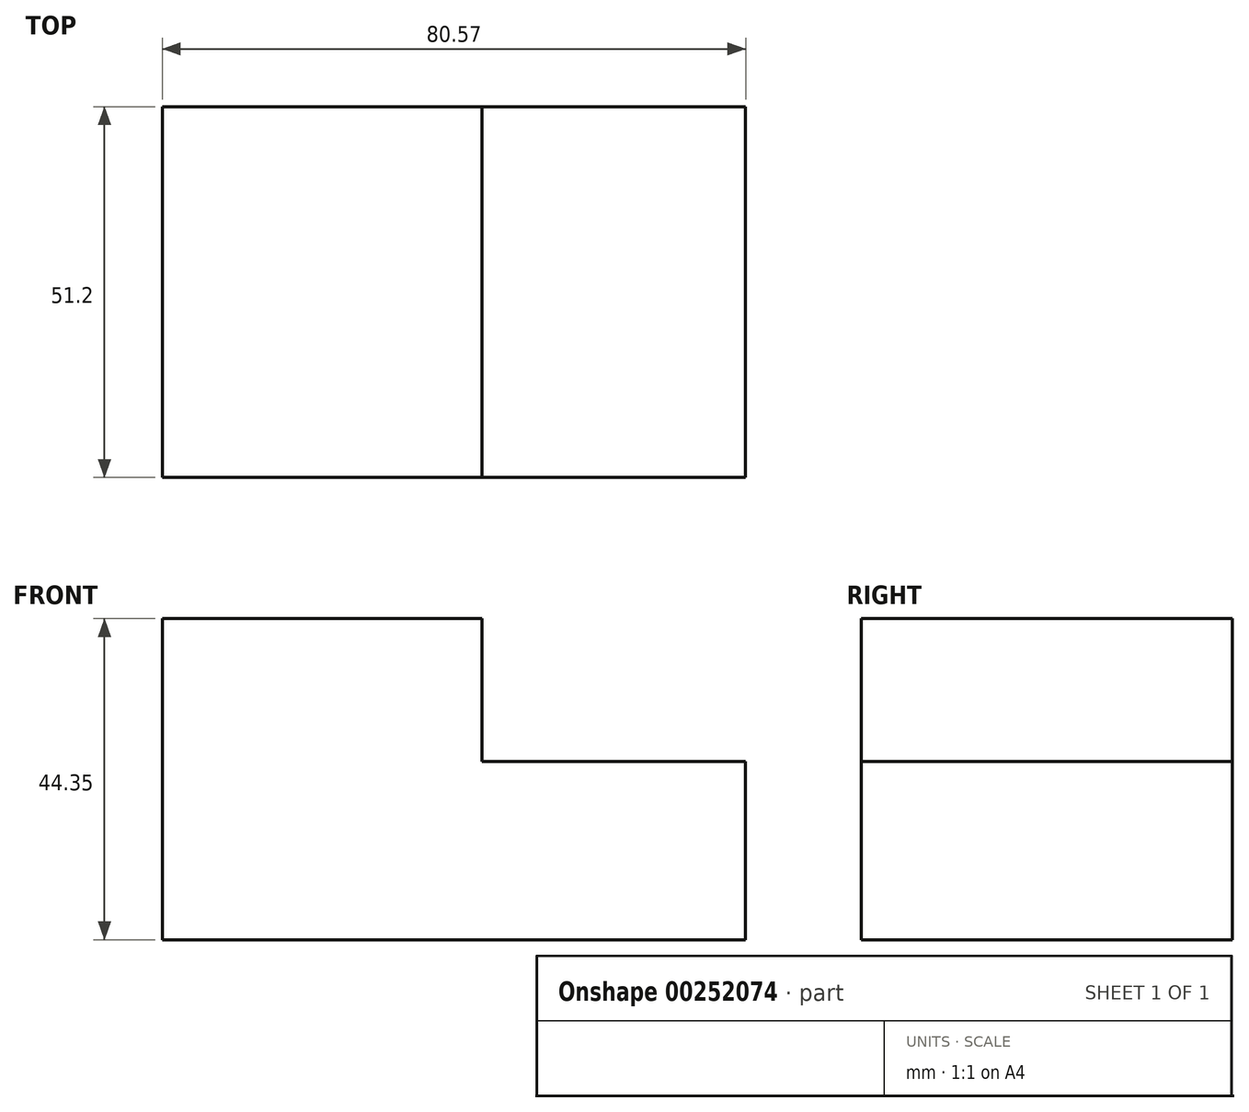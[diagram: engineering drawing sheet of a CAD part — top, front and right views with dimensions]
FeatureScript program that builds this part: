
annotation { "Feature Type Name" : "Feature", "Feature Type Description" : "" }
export const myFeature = defineFeature(function(context is Context, id is Id, definition is map)
    precondition{}
    {
        {
            var Q0;
            Q0=qCreatedBy(makeId("Front.planeOp"),FACE);
            var sketch = newSketch(context, id + "F0", { "sketchPlane" : qUnion([Q0])});
            skLineSegment(sketch, "E0", {"start": v(-34.77, 19.92) * mm, "end": v(-34.77, -24.62) * mm});
            skLineSegment(sketch, "E1", {"start": v(-34.77, -24.62) * mm, "end": v(45.8, -24.62) * mm});
            skLineSegment(sketch, "E2", {"start": v(45.8, -24.62) * mm, "end": v(45.8, 0) * mm});
            skLineSegment(sketch, "E3", {"start": v(45.8, 0) * mm, "end": v(9.4, 0) * mm});
            skLineSegment(sketch, "E4", {"start": v(9.4, 0) * mm, "end": v(9.4, 19.73) * mm});
            skLineSegment(sketch, "E5", {"start": v(9.4, 19.73) * mm, "end": v(-34.77, 19.73) * mm});
            skSolve(sketch);
        }
        {
            var Q0;
            Q0 = qSketchRegion(id + "F0", true);
            extrude(context, id + "F1", {"entities" : qUnion([Q0]), "endBound" : BoundingType.SYMMETRIC, "depth" : 51.2 * mm});
        }
    });
